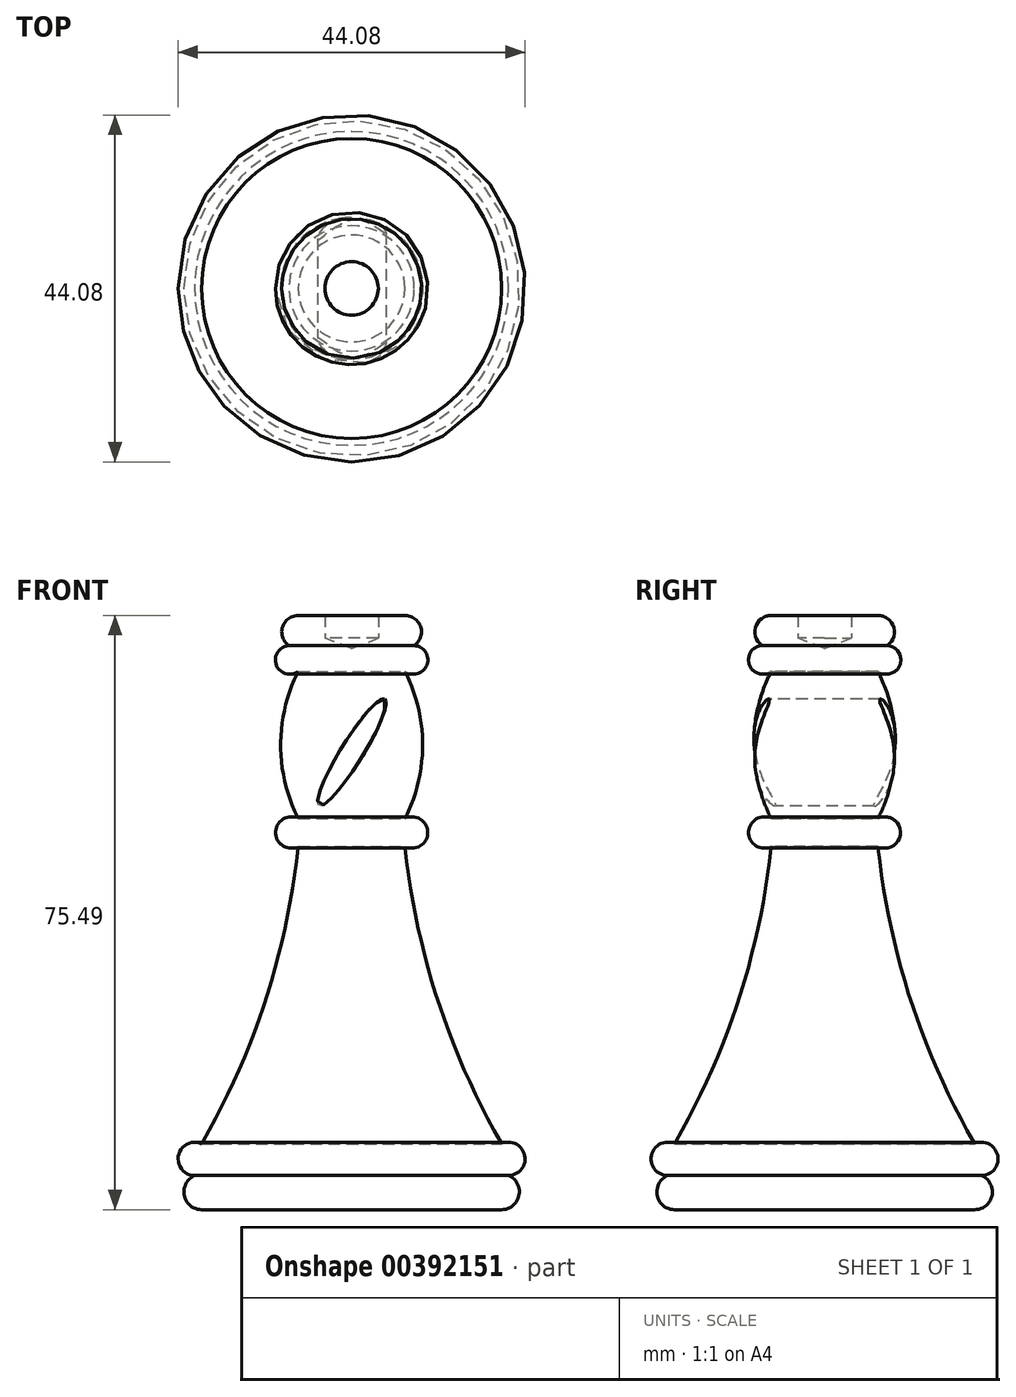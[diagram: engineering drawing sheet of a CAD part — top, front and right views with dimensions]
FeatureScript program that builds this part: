
annotation { "Feature Type Name" : "Feature", "Feature Type Description" : "" }
export const myFeature = defineFeature(function(context is Context, id is Id, definition is map)
    precondition{}
    {
        {
            var Q0;
            Q0=qCreatedBy(makeId("Front.planeOp"),FACE);
            var sketch = newSketch(context, id + "F0", { "sketchPlane" : qUnion([Q0])});
            skLineSegment(sketch, "E0", {"start": v(0, -29.68) * mm, "end": v(0, 33.82) * mm});
            skLineSegment(sketch, "E1", {"start": v(0, -29.68) * mm, "end": v(-19.05, -29.68) * mm});
            skArc(sketch, "E2", {"start": v(-19.05, -25.16) * mm, "mid": v(-21.3, -27.42) * mm, "end": v(-19.05, -29.68) * mm});
            skArc(sketch, "E3", {"start": v(-19.05, -21.3) * mm, "mid": v(-22.04, -23.23) * mm, "end": v(-19.05, -25.16) * mm});
            skArc(sketch, "E4", {"start": v(-19.05, -21.3) * mm, "mid": v(-10.94, -3.06) * mm, "end": v(-6.78, 16.45) * mm});
            skArc(sketch, "E5", {"start": v(-6.78, 20) * mm, "mid": v(-9.66, 18.23) * mm, "end": v(-6.78, 16.45) * mm});
            skArc(sketch, "E6", {"start": v(-6.78, 38.71) * mm, "mid": v(-9.02, 29.36) * mm, "end": v(-6.78, 20) * mm});
            skArc(sketch, "E7", {"start": v(-6.78, 41.62) * mm, "mid": v(-9.69, 40.17) * mm, "end": v(-6.78, 38.71) * mm});
            skLineSegment(sketch, "E8", {"start": v(0, 41.62) * mm, "end": v(0, 33.82) * mm});
            skArc(sketch, "E9", {"start": v(-6.78, 45.81) * mm, "mid": v(-8.87, 43.72) * mm, "end": v(-6.78, 41.62) * mm});
            skLineSegment(sketch, "E10", {"start": v(-6.78, 45.81) * mm, "end": v(-3.39, 45.81) * mm});
            skLineSegment(sketch, "E11", {"start": v(-3.39, 45.81) * mm, "end": v(-3.39, 42.9) * mm});
            skPoint(sketch, "E11.endSnap0", {"position": v(-3.39, 45.81) * mm});
            skLineSegment(sketch, "E12", {"start": v(-3.39, 42.9) * mm, "end": v(0, 41.62) * mm});
            skPoint(sketch, "E13.orphan", {"position": v(0, 45.81) * mm});
            skSolve(sketch);
        }
        {
            var Q0;
            Q0=qSketchRegion(id+"F0",true);
            var Q1;
            Q1=sQuery(id+"F0.wireOp",EDGE,"E0");
            revolve(context, id + "F1", {"entities" : qUnion([Q0]), "axis" : qUnion([Q1]), "revolveType" : RevolveType.FULL});
        }
        {
            var Q0;
            Q0=qCreatedBy(makeId("Front.planeOp"),FACE);
            var sketch = newSketch(context, id + "F2", { "sketchPlane" : qUnion([Q0])});
            skEllipse(sketch, "E14", {"center": v(0, 28.4) * mm, "majorRadius": 7.97 * mm, "minorRadius": 1.4 * mm, "majorAxis": v(0.53, 0.85)});
            skSolve(sketch);
        }
        {
            var Q0;
            Q0=qSketchRegion(id+"F2",true);
            extrude(context, id + "F3", {"entities" : qUnion([Q0]), "operationType" : NewBodyOperationType.REMOVE, "oppositeDirection" : true, "depth" : 25.4 * mm});
        }
        {
            var Q0;
            Q0=qSketchRegion(id+"F2",true);
            extrude(context, id + "F4", {"entities" : qUnion([Q0]), "operationType" : NewBodyOperationType.REMOVE, "depth" : 77.72 * mm});
        }
    });
